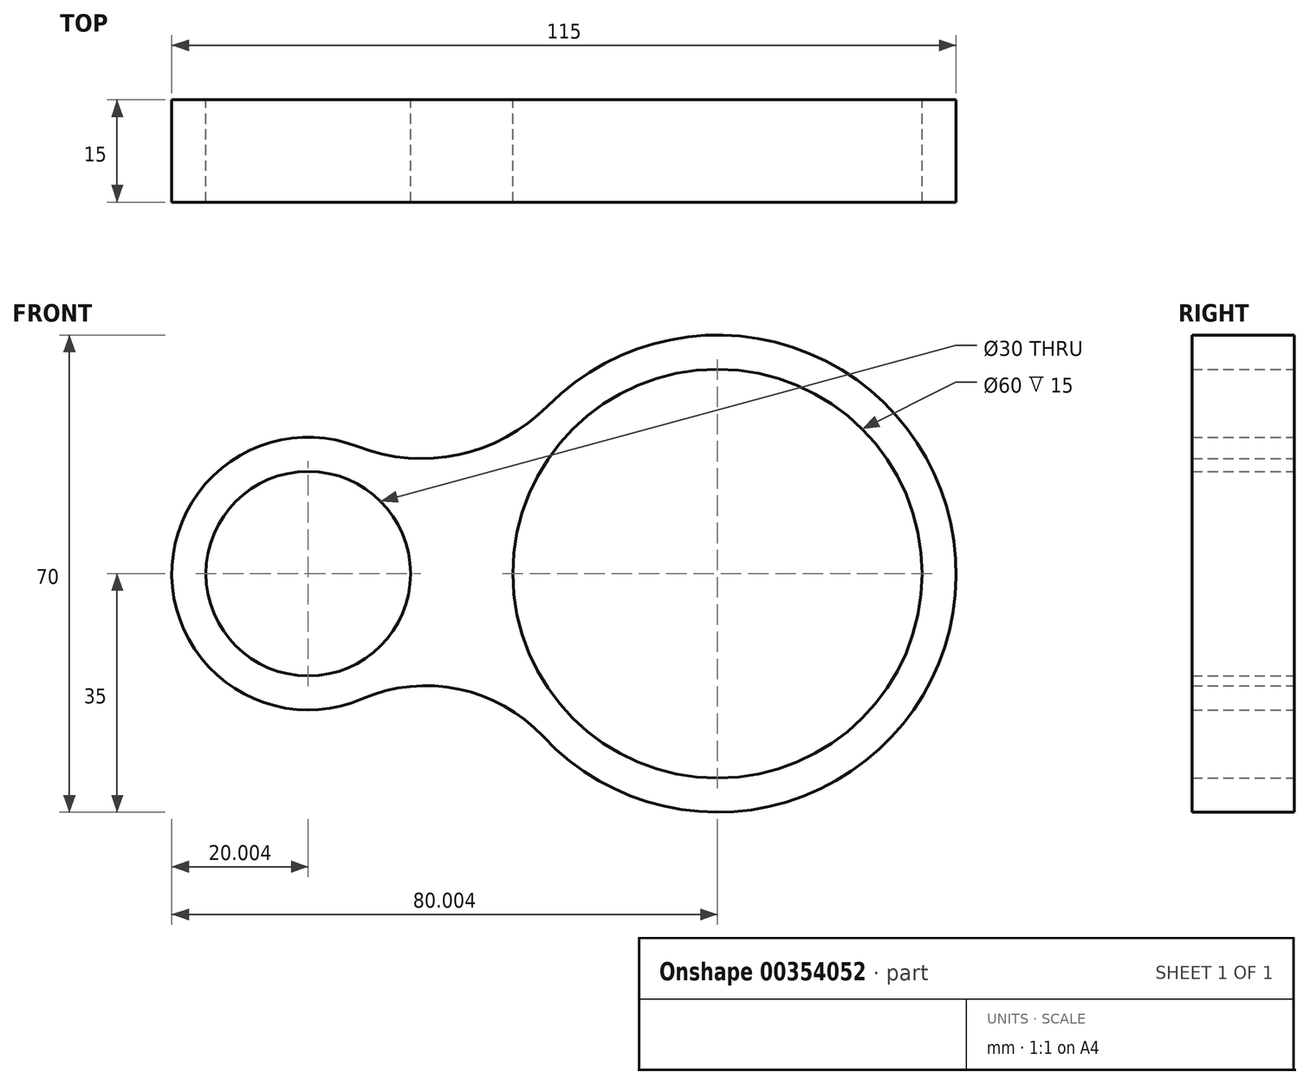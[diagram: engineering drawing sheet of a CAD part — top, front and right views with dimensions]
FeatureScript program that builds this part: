
annotation { "Feature Type Name" : "Feature", "Feature Type Description" : "" }
export const myFeature = defineFeature(function(context is Context, id is Id, definition is map)
    precondition{}
    {
        {
            var Q0;
            Q0=qCreatedBy(makeId("Front.planeOp"),FACE);
            var sketch = newSketch(context, id + "F0", { "sketchPlane" : qUnion([Q0])});
            skCircle(sketch, "E0", {"center": v(-31.1, 0) * mm, "radius": 20 * mm});
            skCircle(sketch, "E1", {"center": v(-31.1, 0) * mm, "radius": 15 * mm});
            skCircle(sketch, "E2", {"center": v(28.9, 0) * mm, "radius": 35 * mm});
            skCircle(sketch, "E3", {"center": v(28.9, 0) * mm, "radius": 30 * mm});
            skArc(sketch, "E4", {"start": v(-23.85, 18.64) * mm, "mid": v(-9.04, 17.45) * mm, "end": v(4, 24.6) * mm});
            skArc(sketch, "E5", {"start": v(3.34, -23.9) * mm, "mid": v(-9.04, -16.94) * mm, "end": v(-23.18, -18.36) * mm});
            skSolve(sketch);
        }
        {
            var Q0;
            Q0 = qSketchRegion(id + "F0", true);
            extrude(context, id + "F1", {"entities" : qUnion([Q0]), "depth" : 15 * mm});
        }
    });
